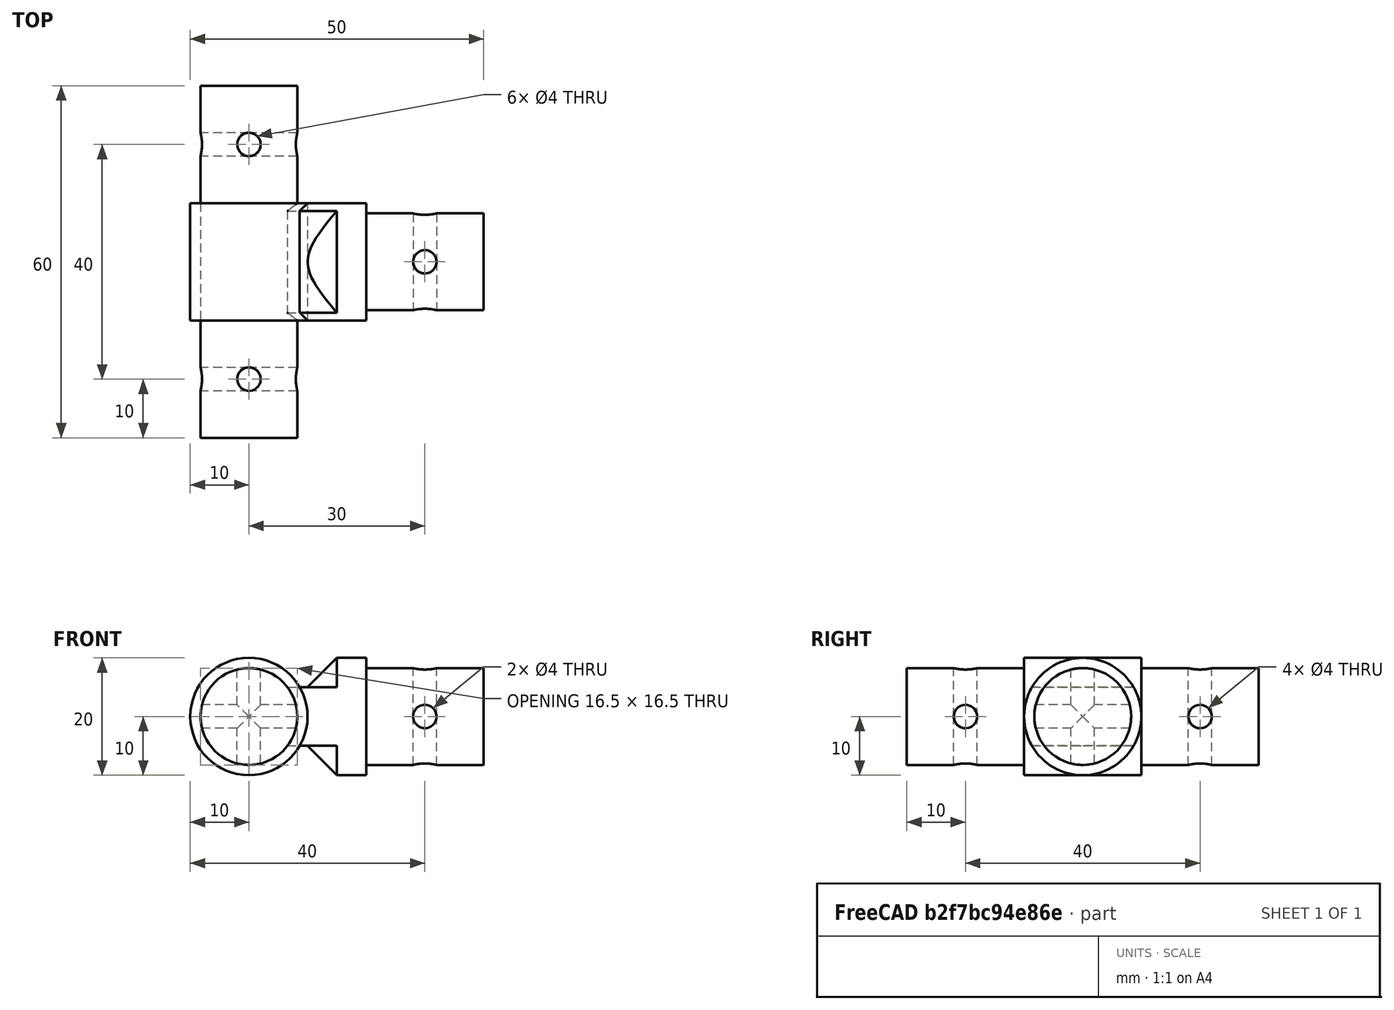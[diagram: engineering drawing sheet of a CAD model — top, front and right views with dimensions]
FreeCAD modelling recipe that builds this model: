
FCSTD DOCUMENT  (FreeCAD 0.18R16110 (Git))
Label: RailT
License: All rights reserved
LicenseURL: http://en.wikipedia.org/wiki/All_rights_reserved
objects: Part::Cylinder×11, Part::MultiFuse×2, Part::Box×1, Part::Cone×1, Part::MultiCommon×1, Part::Cut×1
note: 17 computed .brp shape members not serialized (recipe doc carries the construction recipe); baked Part::Feature solids carry a one-line shape summary decoded from their .brp

FEATURE [Part::Cylinder] Cylinder003
  Angle = 360
  AttacherType = Attacher::AttachEngine3D
  Height = 20
  Placement = pos=(0,10,4.2e-15) rot=(0,0.707107,-0.707107;3.14159rad)
  Radius = 10
FEATURE [Part::Cylinder] Cylinder004
  Angle = 360
  AttacherType = Attacher::AttachEngine3D
  Height = 60
  Placement = pos=(0,30,8.7e-15) rot=(0,0.707107,-0.707107;3.14159rad)
  Radius = 8.25
FEATURE [Part::Cylinder] Cylinder005
  Angle = 360
  AttacherType = Attacher::AttachEngine3D
  Height = 20
  Placement = pos=(20,4e-15,2e-15) rot=(0.57735,-0.57735,0.57735;4.18879rad)
  Radius = 8.25
FEATURE [Part::Box] Box  label="Cube"
  AttacherType = Attacher::AttachEngine3D
  Height = 10
  Length = 20
  Placement = pos=(0,-10,-5) rot=(0,0,1;0rad)
  Width = 20
FEATURE [Part::Cone] Cone
  Angle = 360
  AttacherType = Attacher::AttachEngine3D
  Height = 10
  Placement = pos=(5,0,1.1e-15) rot=(0,1,0;1.5708rad)
  Radius1 = 0
  Radius2 = 10
FEATURE [Part::Cylinder] Cylinder
  Angle = 360
  AttacherType = Attacher::AttachEngine3D
  Height = 20
  Placement = pos=(0,0,0) rot=(0,1,0;1.5708rad)
  Radius = 10
FEATURE [Part::MultiCommon] Common
  Shapes = -> [Box,Cylinder]
FEATURE [Part::Cylinder] Cylinder006
  Angle = 360
  AttacherType = Attacher::AttachEngine3D
  Height = 5
  Placement = pos=(15,0,3e-15) rot=(0,1,0;1.5708rad)
  Radius = 10
FEATURE [Part::MultiFuse] Fusion  label="Positive Fusion"
  Shapes = -> [Cylinder005,Cylinder004,Cylinder003,Cone,Cylinder006,Common]
FEATURE [Part::Cylinder] Cylinder007
  Angle = 360
  AttacherType = Attacher::AttachEngine3D
  Height = 20
  Placement = pos=(0,-20,-10) rot=(0,0,1;0rad)
  Radius = 2
FEATURE [Part::Cylinder] Cylinder008
  Angle = 360
  AttacherType = Attacher::AttachEngine3D
  Height = 20
  Placement = pos=(0,20,-10) rot=(0,0,1;0rad)
  Radius = 2
FEATURE [Part::Cylinder] Cylinder009
  Angle = 360
  AttacherType = Attacher::AttachEngine3D
  Height = 20
  Placement = pos=(30,0,-10) rot=(0,0,1;0rad)
  Radius = 2
FEATURE [Part::Cylinder] Cylinder010
  Angle = 360
  AttacherType = Attacher::AttachEngine3D
  Height = 20
  Placement = pos=(10,-20,4.9e-15) rot=(-0.57735,0.57735,0.57735;4.18879rad)
  Radius = 2
FEATURE [Part::Cylinder] Cylinder011
  Angle = 360
  AttacherType = Attacher::AttachEngine3D
  Height = 20
  Placement = pos=(30,10,-1.8e-15) rot=(1,0,0;1.5708rad)
  Radius = 2
FEATURE [Part::Cylinder] Cylinder012
  Angle = 360
  AttacherType = Attacher::AttachEngine3D
  Height = 20
  Placement = pos=(10,20,5e-15) rot=(0.57735,-0.57735,-0.57735;2.0944rad)
  Radius = 2
FEATURE [Part::MultiFuse] Fusion001  label="Negative Fusion"
  Shapes = -> [Cylinder007,Cylinder012,Cylinder009,Cylinder010,Cylinder008,Cylinder011]
FEATURE [Part::Cut] Cut
  Base = -> Fusion
  Tool = -> Fusion001
